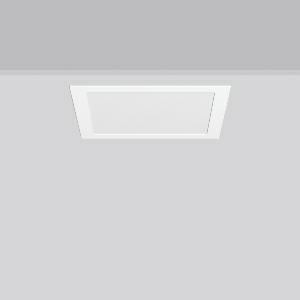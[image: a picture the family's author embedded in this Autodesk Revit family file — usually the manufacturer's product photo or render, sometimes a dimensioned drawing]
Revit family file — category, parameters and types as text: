
# Revit family: toledo_flat_square_e_672244_002_1_5cb5
name_source: partatom
category: Lighting Fixtures
units: mm (PartAtom-declared; Revit-internal decimal feet)

## family parameters
Cut with Voids When Loaded = No
Host = Face
Light Source = No
Part Type = Normal
Room Calculation Point = No
Round Connector Dimension = Use Diameter
Shared = No

## types (1)
- TOLEDO FLAT square E (1 x LED Modul 840, 2200 lm, 4000)
    Apparent Load = 22 VA
    CIE Flux Codes = 49 80 96 100 100
    Color Rendering = 80
    Color Temperature = 4000
    Default Elevation = 1800 mm
    Description = Series: TOLEDO FLAT square
Square recessed downlight. For escape route illumination. Housing: die-cast aluminium, powder-coated. Lightguide and diffuser made of non-yellowing plastic (PMMA). Diffuser opal matt plastic. Ceiling installation with spring system. Including separate LED converter with connecting cable 250 mm. Suitable for connection to central battery systems. External driver with simple plug-in locking system. 
Colour: white
Length: 300 mm
Width: 300 mm
Height: 3 mm
Cut-out length: 280 mm
Cut-out width: 280 mm
Recess height: 35 mm
Luminaire: recess height: 31-51 mm
Weight: 1.2 kg
Operating mode: maintained power mode
Lamp: LED
Socket: without socket
Colour temperature: 4000K
Colour rendering index (CRI): 80
System power: 22 W
Rated luminous flux: 2200 lm
Luminous flux, emergency: 2200 lm
System power, emergency: 22 W
Control gear: Regulated power supply
Protection class: II
Type of protection: IP 54
    Height = 0 mm  [stored 0 ft]
    Lamp = 1 x LED Modul 840
    Lamp Light Flux = 2200 lm
    Lamp count = 1
    Length = 300 mm
    Lifetime = 50000 h
    Luminous efficacy = 100 lm/W
    Manufacturer = RZB
    ModVariant = No
    Model = 672244.002.1
    Mounting Place = Ceiling
    Mounting Type = Recessed
    Number of Poles = 1
    OnlyDefault = Yes
    Power Factor = 1
    Product Name = TOLEDO FLAT square E
    Product group = Recessed downlights
    ProductGroupID = 402
    Protection Class = Protection class II
    Protection Degree = IP 40
    RLX_Detail_Level = 1
    RLX_Emergency_Light_Flux = 2200 lm
    RLX_Emergency_Type = 3
    RLX_Emergency_Type_DB = Yes
    RlxData = <blob elided: 12809 chars, md5=d7dd981d>
    Socket = socket
    Standby Power = 0 W
    System Light Flux = 2200 lm
    System Power = 22 W
    Type Comments = Product without accessories
    Type Image = 901488.002.jpg
    URL = http://relux.com
    VarID = ---
    Voltage = 230 V
    Voltage Range = 220-240 V
    Weight = 0.00 kg
    Width = 300 mm

note: [stored X ft] marks values corroborated as IEEE doubles in the binary element streams (Revit-internal decimal feet)

## geometry (parser evidence)
native form markers: Sweep x9
no freeform markers — native parametric forms only
